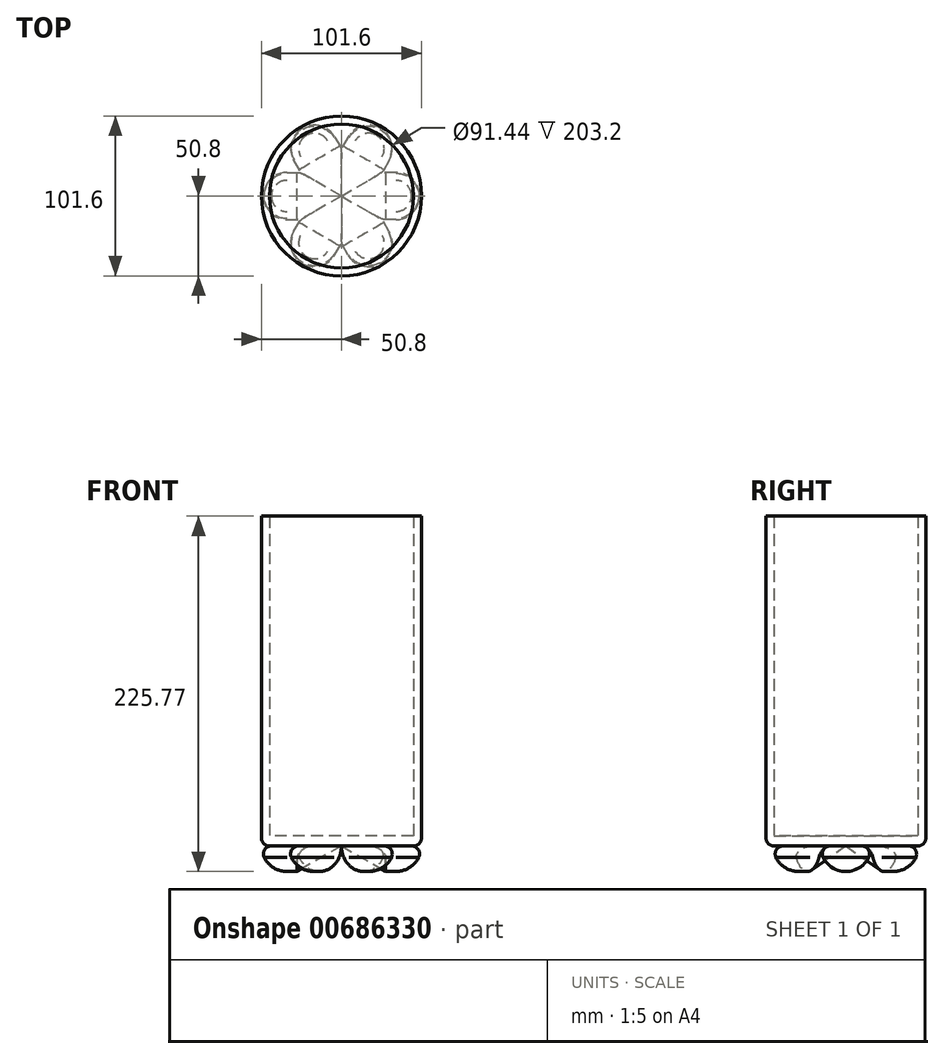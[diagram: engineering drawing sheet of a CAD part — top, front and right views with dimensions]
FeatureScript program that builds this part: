
annotation { "Feature Type Name" : "Feature", "Feature Type Description" : "" }
export const myFeature = defineFeature(function(context is Context, id is Id, definition is map)
    precondition{}
    {
        {
            var Q0;
            Q0=qCreatedBy(makeId("Top.planeOp"),FACE);
            var sketch = newSketch(context, id + "F0", { "sketchPlane" : qUnion([Q0])});
            skLineSegment(sketch, "E0", {"start": v(0, 0) * mm, "end": v(28.1, -16.22) * mm});
            skLineSegment(sketch, "E1", {"start": v(0, 0) * mm, "end": v(50.8, 0) * mm});
            skLineSegment(sketch, "E2", {"start": v(28.1, -16.22) * mm, "end": v(34.58, -16.22) * mm});
            skArc(sketch, "E3", {"start": v(34.58, -16.22) * mm, "mid": v(46.05, -11.47) * mm, "end": v(50.8, 0) * mm});
            skSolve(sketch);
        }
        {
            var Q0;
            Q0=makeQuery(id+"F0.imprint","IMPRINT",FACE,{"disambiguationData":[TD([[makeQuery(id+"F0.imprint","IMPRINT",EDGE,{"derivedFrom":sQuery(id+"F0.wireOp",EDGE,"E0")}),1.0]])]});
            var Q1;
            Q1=sQuery(id+"F0.wireOp",EDGE,"E1");
            revolve(context, id + "F1", {"entities" : qUnion([Q0]), "axis" : qUnion([Q1]), "revolveType" : RevolveType.ONE_DIRECTION, "angle" : 180 * degree});
        }
        {
            var Q0;
            Q0=qCreatedBy(makeId("Front.planeOp"),FACE);
            var sketch = newSketch(context, id + "F2", { "sketchPlane" : qUnion([Q0])});
            skLineSegment(sketch, "E4", {"start": v(0, 0) * mm, "end": v(0, 24.62) * mm});
            skSolve(sketch);
        }
        {
            var Q0;
            Q0=makeQuery(id+"F1.opRevolve","SWEPT_BODY",BODY,{"disambiguationData":[OSD([sQuery(id+"F0.wireOp",EDGE,"E0"),sQuery(id+"F0.wireOp",EDGE,"E1"),sQuery(id+"F0.wireOp",EDGE,"E2"),sQuery(id+"F0.wireOp",EDGE,"E3")])]});
            var Q1;
            Q1=sQuery(id+"F2.wireOp",EDGE,"E4");
            circularPattern(context, id + "F3", {"entities" : qUnion([Q0]), "axis" : qUnion([Q1]), "angle" : 360 * degree, "instanceCount" : 6, "equalSpace" : true});
        }
        {
            var Q0;
            Q0=qCreatedBy(makeId("Top.planeOp"),FACE);
            var sketch = newSketch(context, id + "F4", { "sketchPlane" : qUnion([Q0])});
            skCircle(sketch, "E5", {"center": v(0, 0) * mm, "radius": 50.8 * mm});
            skSolve(sketch);
        }
        {
            var Q0;
            Q0=makeQuery(id+"F4.imprint","IMPRINT",FACE,{"disambiguationData":[TD([[makeQuery(id+"F4.imprint","IMPRINT",EDGE,{"derivedFrom":sQuery(id+"F4.wireOp",EDGE,"E5")}),1.0]])]});
            extrude(context, id + "F5", {"entities" : qUnion([Q0]), "depth" : 6.35 * mm, "offsetDistance" : 25.4 * mm});
        }
        {
            var Q0;
            Q0=makeQuery(id+"F5.opExtrude","CAP_FACE",FACE,{"disambiguationData":[OSD([sQuery(id+"F4.wireOp",EDGE,"E5")])],"isStart":false});
            var sketch = newSketch(context, id + "F6", { "sketchPlane" : qUnion([Q0])});
            skCircle(sketch, "E6", {"center": v(0, 0) * mm, "radius": 50.8 * mm});
            skCircle(sketch, "E7", {"center": v(0, 0) * mm, "radius": 45.72 * mm});
            skSolve(sketch);
        }
        {
            var Q0;
            Q0 = qSketchRegion(id + "F6", true);
            extrude(context, id + "F7", {"entities" : qUnion([Q0]), "operationType" : NewBodyOperationType.ADD, "depth" : 203.2 * mm, "offsetDistance" : 25.4 * mm});
        }
        {
            var Q0;
            Q0=makeQuery(id+"F5.opExtrude","CAP_EDGE",EDGE,{"disambiguationData":[OSD([sQuery(id+"F4.wireOp",EDGE,"E5")])],"isStart":true});
            fillet(context, id + "F8", {"entities" : qUnion([Q0]), "radius" : 5.08 * mm, "tangentPropagation" : true, "allowEdgeOverflow" : false});
        }
        {
            var Q0;
            Q0=makeQuery(id+"F3.opPattern","COPY",EDGE,{"derivedFrom":makeQuery(id+"F1.opRevolve","CAP_EDGE",EDGE,{"disambiguationData":[OSD([sQuery(id+"F0.wireOp",EDGE,"E3")])],"isStart":false}),"instanceName":"5"});
            fillet(context, id + "F9", {"entities" : qUnion([Q0]), "radius" : 5.08 * mm, "tangentPropagation" : true, "allowEdgeOverflow" : false});
        }
        {
            var Q0;
            Q0=makeQuery(id+"F3.opPattern","COPY",EDGE,{"derivedFrom":makeQuery(id+"F1.opRevolve","CAP_EDGE",EDGE,{"disambiguationData":[OSD([sQuery(id+"F0.wireOp",EDGE,"E3")])],"isStart":false}),"instanceName":"4"});
            var Q1;
            Q1=makeQuery(id+"F1.opRevolve","CAP_EDGE",EDGE,{"disambiguationData":[OSD([sQuery(id+"F0.wireOp",EDGE,"E3")])],"isStart":false});
            var Q2;
            Q2=makeQuery(id+"F3.opPattern","COPY",EDGE,{"derivedFrom":makeQuery(id+"F1.opRevolve","CAP_EDGE",EDGE,{"disambiguationData":[OSD([sQuery(id+"F0.wireOp",EDGE,"E3")])],"isStart":false}),"instanceName":"1"});
            var Q3;
            Q3=makeQuery(id+"F3.opPattern","COPY",EDGE,{"derivedFrom":makeQuery(id+"F1.opRevolve","CAP_EDGE",EDGE,{"disambiguationData":[OSD([sQuery(id+"F0.wireOp",EDGE,"E3")])],"isStart":false}),"instanceName":"2"});
            var Q4;
            Q4=makeQuery(id+"F3.opPattern","COPY",EDGE,{"derivedFrom":makeQuery(id+"F1.opRevolve","CAP_EDGE",EDGE,{"disambiguationData":[OSD([sQuery(id+"F0.wireOp",EDGE,"E3")])],"isStart":false}),"instanceName":"3"});
            fillet(context, id + "F10", {"entities" : qUnion([Q0, Q1, Q2, Q3, Q4]), "radius" : 5.08 * mm, "tangentPropagation" : true, "allowEdgeOverflow" : false});
        }
    });
